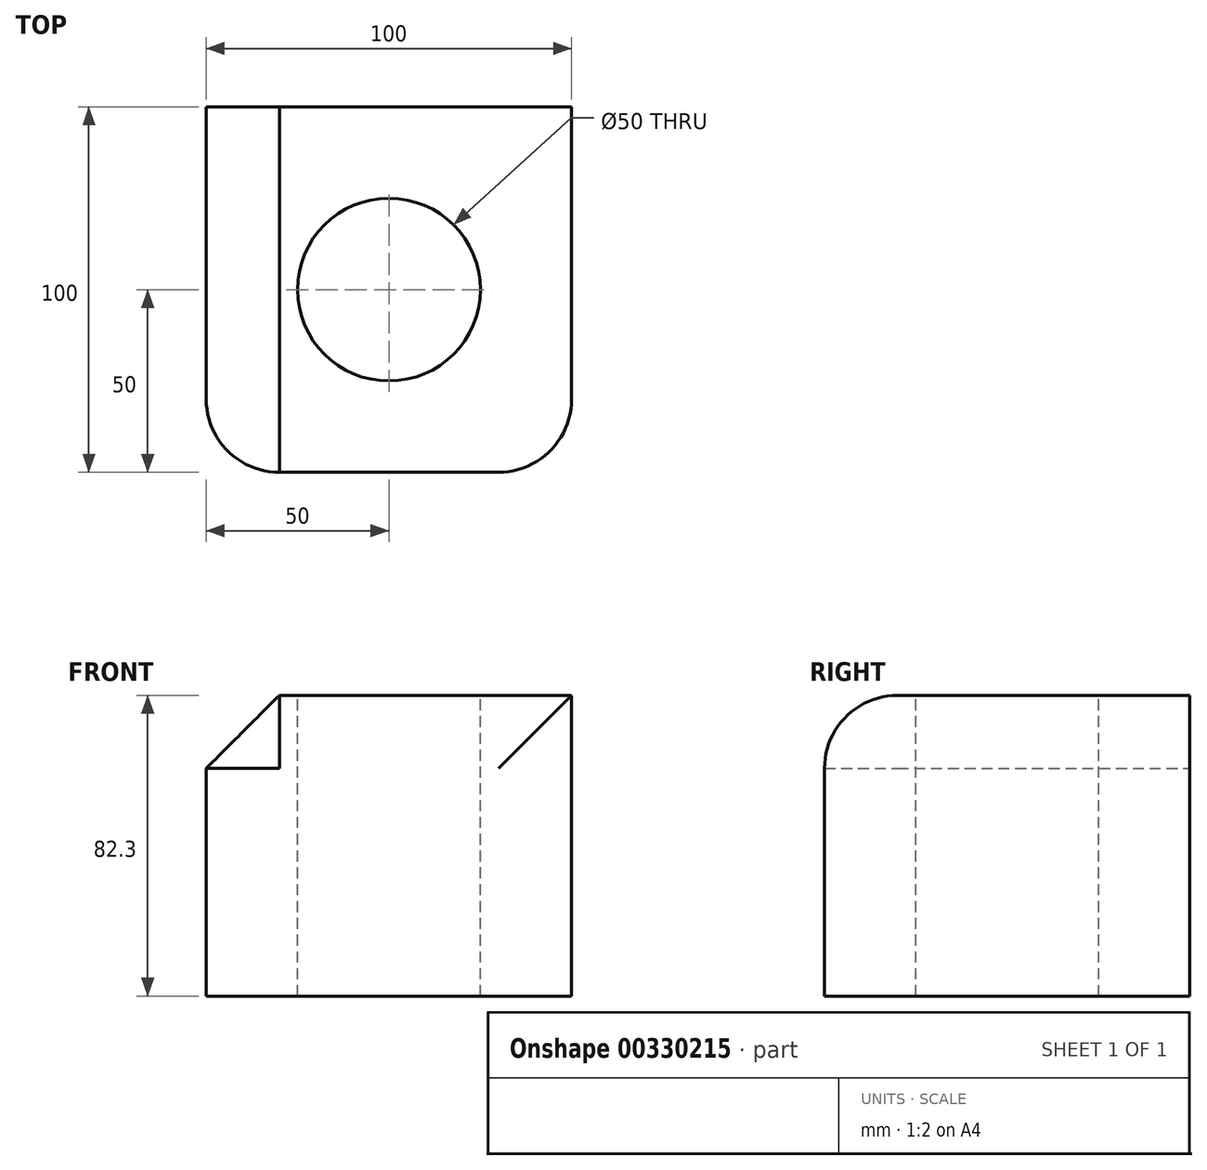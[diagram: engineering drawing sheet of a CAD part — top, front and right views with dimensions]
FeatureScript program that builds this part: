
annotation { "Feature Type Name" : "Feature", "Feature Type Description" : "" }
export const myFeature = defineFeature(function(context is Context, id is Id, definition is map)
    precondition{}
    {
        {
            var Q0;
            Q0=qCreatedBy(makeId("Top.planeOp"),FACE);
            var sketch = newSketch(context, id + "F0", { "sketchPlane" : qUnion([Q0])});
            skLineSegment(sketch, "E0.bottom", {"start": v(50, -50) * mm, "end": v(-50, -50) * mm});
            skLineSegment(sketch, "E0.top", {"start": v(50, 50) * mm, "end": v(-50, 50) * mm});
            skLineSegment(sketch, "E0.left", {"start": v(50, -50) * mm, "end": v(50, 50) * mm});
            skLineSegment(sketch, "E0.right", {"start": v(-50, -50) * mm, "end": v(-50, 50) * mm});
            skPoint(sketch, "E0.middle", {"position": v(0, 0) * mm});
            skSolve(sketch);
        }
        {
            var Q0;
            Q0=makeQuery(id+"F0.imprint","IMPRINT",FACE,{"disambiguationData":[TD([[makeQuery(id+"F0.imprint","IMPRINT",EDGE,{"derivedFrom":sQuery(id+"F0.wireOp",EDGE,"E0.bottom")}),-1.0]])]});
            extrude(context, id + "F1", {"entities" : qUnion([Q0]), "depth" : 82.3 * mm});
        }
        {
            var Q0;
            Q0=makeQuery(id+"F1.opExtrude","CAP_FACE",FACE,{"disambiguationData":[OSD([sQuery(id+"F0.wireOp",EDGE,"E0.bottom"),sQuery(id+"F0.wireOp",EDGE,"E0.top"),sQuery(id+"F0.wireOp",EDGE,"E0.left"),sQuery(id+"F0.wireOp",EDGE,"E0.right")])],"isStart":false});
            var sketch = newSketch(context, id + "F2", { "sketchPlane" : qUnion([Q0])});
            skCircle(sketch, "E1", {"center": v(0, 0) * mm, "radius": 25 * mm});
            skSolve(sketch);
        }
        {
            var Q0;
            Q0=makeQuery(id+"F2.imprint","IMPRINT",FACE,{"disambiguationData":[TD([[makeQuery(id+"F2.imprint","IMPRINT",EDGE,{"derivedFrom":sQuery(id+"F2.wireOp",EDGE,"E1")}),1.0]])]});
            extrude(context, id + "F3", {"entities" : qUnion([Q0]), "operationType" : NewBodyOperationType.REMOVE, "endBound" : BoundingType.THROUGH_ALL, "oppositeDirection" : true, "depth" : 25 * mm});
        }
        {
            var Q0;
            Q0=makeQuery(id+"F1.opExtrude","SWEPT_EDGE",EDGE,{"disambiguationData":[OSD([sQuery(id+"F0.wireOp",EDGE,"E0.bottom"),sQuery(id+"F0.wireOp",EDGE,"E0.right")])]});
            var Q1;
            Q1=makeQuery(id+"F1.opExtrude","SWEPT_EDGE",EDGE,{"disambiguationData":[OSD([sQuery(id+"F0.wireOp",EDGE,"E0.bottom"),sQuery(id+"F0.wireOp",EDGE,"E0.left")])]});
            var Q2;
            Q2=makeQuery(id+"F1.opExtrude","CAP_EDGE",EDGE,{"disambiguationData":[OSD([sQuery(id+"F0.wireOp",EDGE,"E0.bottom")])],"isStart":false});
            fillet(context, id + "F4", {"entities" : qUnion([Q0, Q1, Q2]), "radius" : 20 * mm, "tangentPropagation" : true, "allowEdgeOverflow" : false});
        }
        {
            var Q0;
            Q0=makeQuery(id+"F1.opExtrude","CAP_EDGE",EDGE,{"disambiguationData":[OSD([sQuery(id+"F0.wireOp",EDGE,"E0.right")])],"isStart":false});
            chamfer(context, id + "F5", {"entities" : qUnion([Q0]), "width" : 20 * mm, "tangentPropagation" : true});
        }
    });
